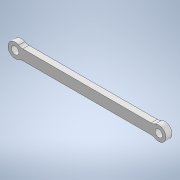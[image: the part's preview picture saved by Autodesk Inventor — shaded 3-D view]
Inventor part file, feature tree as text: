
AUTODESK INVENTOR PART (.ipt)
format: ipt  version: 2020 (Build 240168000, 168)  size: 124,928 bytes
history: native  units: mm
features: extrude x1, fillet x1, sketch x1
ambient origin geometry x8: Origin, YZ Plane, XZ Plane, XY Plane, X Axis, Y Axis, Z Axis, Center Point
bodies: Solid1 (feature_tree)
feature tree (3):
  extrude  "Extrusion1"  Depth=2.0mm
  fillet  "Fillet2"  Radius=1.5mm
  sketch  "Sketch1"  dims[d0=1.8mm d1=3.5mm d4=1.5mm d5=0.0mm d8=2.5mm d9=32.6mm d10=2.0mm]
